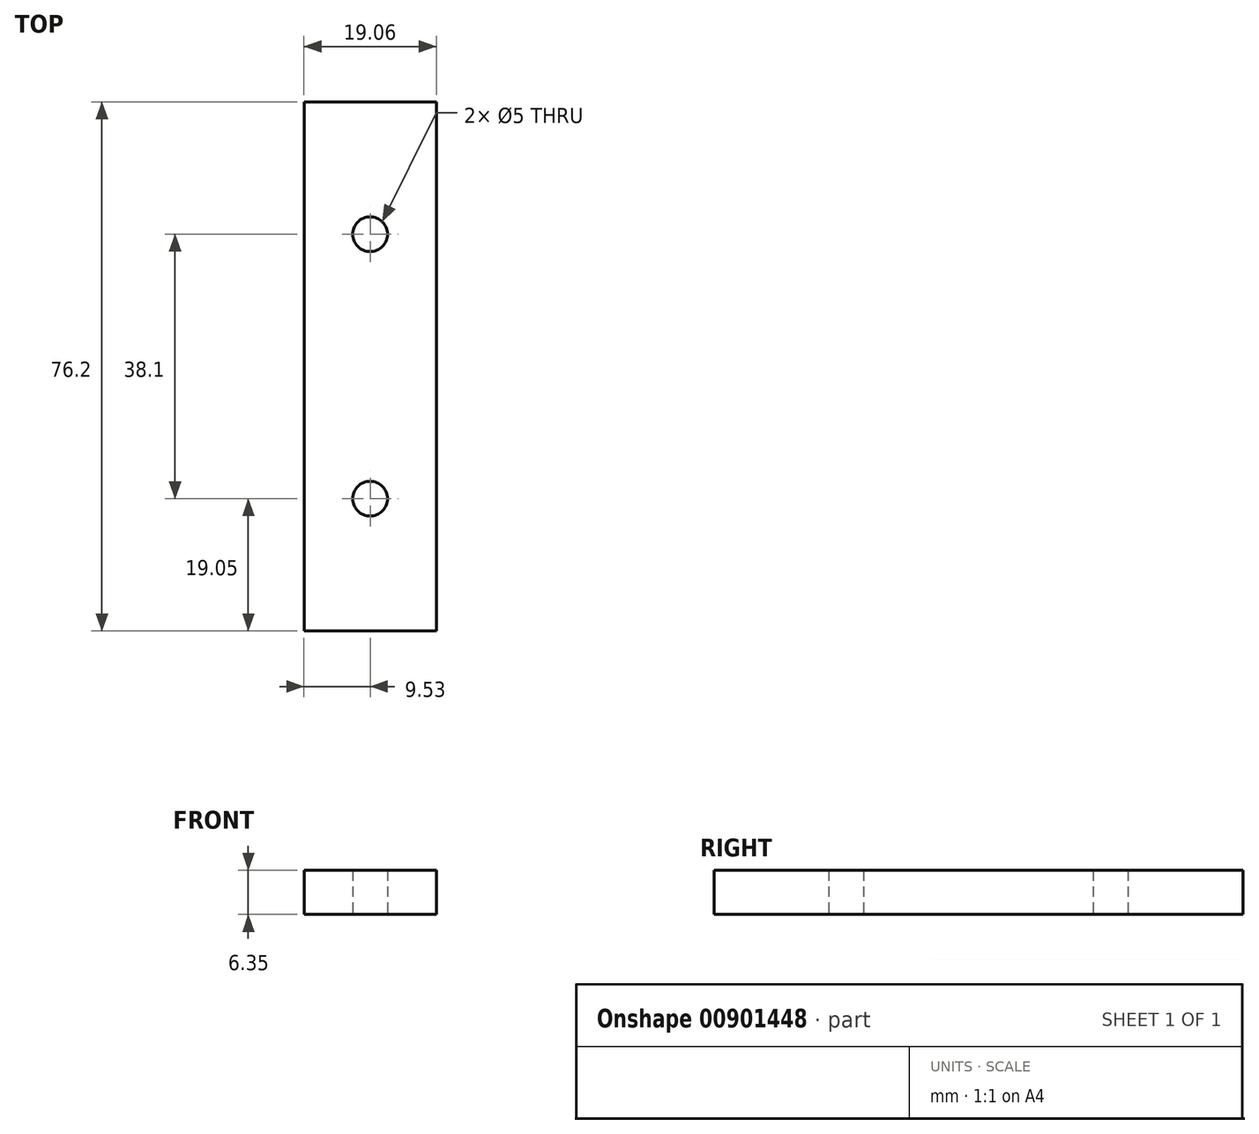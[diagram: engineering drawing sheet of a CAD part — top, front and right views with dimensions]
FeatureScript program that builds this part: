
annotation { "Feature Type Name" : "Feature", "Feature Type Description" : "" }
export const myFeature = defineFeature(function(context is Context, id is Id, definition is map)
    precondition{}
    {
        {
            var Q0;
            Q0=qCreatedBy(makeId("Top.planeOp"),FACE);
            var sketch = newSketch(context, id + "F0", { "sketchPlane" : qUnion([Q0])});
            skLineSegment(sketch, "E0.bottom", {"start": v(9.53, -38.1) * mm, "end": v(-9.52, -38.1) * mm});
            skLineSegment(sketch, "E0.top", {"start": v(9.53, 38.1) * mm, "end": v(-9.52, 38.1) * mm});
            skLineSegment(sketch, "E0.left", {"start": v(9.53, -38.1) * mm, "end": v(9.53, 38.1) * mm});
            skLineSegment(sketch, "E0.right", {"start": v(-9.52, -38.1) * mm, "end": v(-9.52, 38.1) * mm});
            skPoint(sketch, "E0.middle", {"position": v(0, 0) * mm});
            skCircle(sketch, "E1", {"center": v(0, 19.05) * mm, "radius": 2.5 * mm});
            skCircle(sketch, "E2.MirrorC", {"center": v(0, -19.05) * mm, "radius": 2.5 * mm});
            skSolve(sketch);
        }
        {
            var Q0;
            Q0 = qSketchRegion(id + "F0", true);
            extrude(context, id + "F1", {"entities" : qUnion([Q0]), "depth" : 6.35 * mm, "offsetDistance" : 25.4 * mm});
        }
    });
